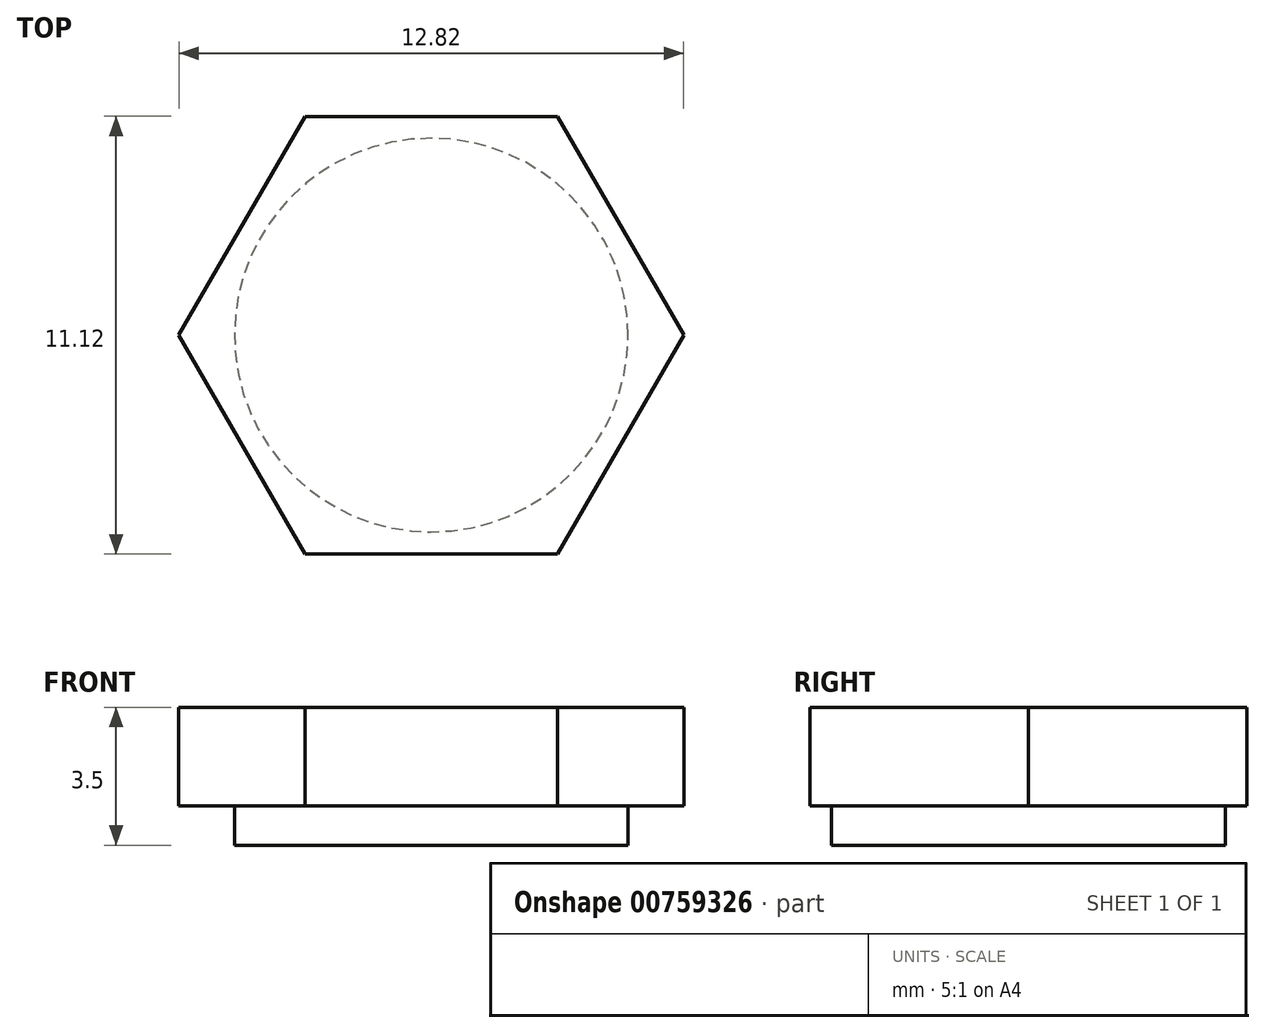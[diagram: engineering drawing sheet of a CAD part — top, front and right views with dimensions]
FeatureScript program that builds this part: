
annotation { "Feature Type Name" : "Feature", "Feature Type Description" : "" }
export const myFeature = defineFeature(function(context is Context, id is Id, definition is map)
    precondition{}
    {
        {
            var Q0;
            Q0=qCreatedBy(makeId("Top.planeOp"),FACE);
            var sketch = newSketch(context, id + "F0", { "sketchPlane" : qUnion([Q0])});
            skLineSegment(sketch, "E0", {"start": v(-3.2, -5.55) * mm, "end": v(3.2, -5.55) * mm});
            skLineSegment(sketch, "E1", {"start": v(3.2, -5.55) * mm, "end": v(6.41, 0) * mm});
            skLineSegment(sketch, "E2", {"start": v(6.41, 0) * mm, "end": v(3.2, 5.56) * mm});
            skLineSegment(sketch, "E3", {"start": v(3.2, 5.55) * mm, "end": v(-3.2, 5.55) * mm});
            skLineSegment(sketch, "E4", {"start": v(-3.2, 5.55) * mm, "end": v(-6.41, 0) * mm});
            skLineSegment(sketch, "E5", {"start": v(-6.41, 0) * mm, "end": v(-3.2, -5.56) * mm});
            skCircle(sketch, "E6", {"center": v(0, 0) * mm, "radius": 5 * mm});
            skSolve(sketch);
        }
        {
            var Q0;
            Q0=makeQuery(id+"F0.imprint","IMPRINT",FACE,{"disambiguationData":[TD([[makeQuery(id+"F0.imprint","IMPRINT",EDGE,{"derivedFrom":sQuery(id+"F0.wireOp",EDGE,"E0")}),1.0]])]});
            var Q1;
            Q1=makeQuery(id+"F0.imprint","IMPRINT",FACE,{"disambiguationData":[TD([[makeQuery(id+"F0.imprint","IMPRINT",EDGE,{"derivedFrom":sQuery(id+"F0.wireOp",EDGE,"E6")}),1.0]])]});
            extrude(context, id + "F1", {"entities" : qUnion([Q0, Q1]), "depth" : 2.5 * mm, "offsetDistance" : 25 * mm});
        }
        {
            var Q0;
            Q0=makeQuery(id+"F0.imprint","IMPRINT",FACE,{"disambiguationData":[TD([[makeQuery(id+"F0.imprint","IMPRINT",EDGE,{"derivedFrom":sQuery(id+"F0.wireOp",EDGE,"E6")}),1.0]])]});
            extrude(context, id + "F2", {"entities" : qUnion([Q0]), "operationType" : NewBodyOperationType.ADD, "oppositeDirection" : true, "depth" : 1 * mm, "offsetDistance" : 25 * mm});
        }
    });
